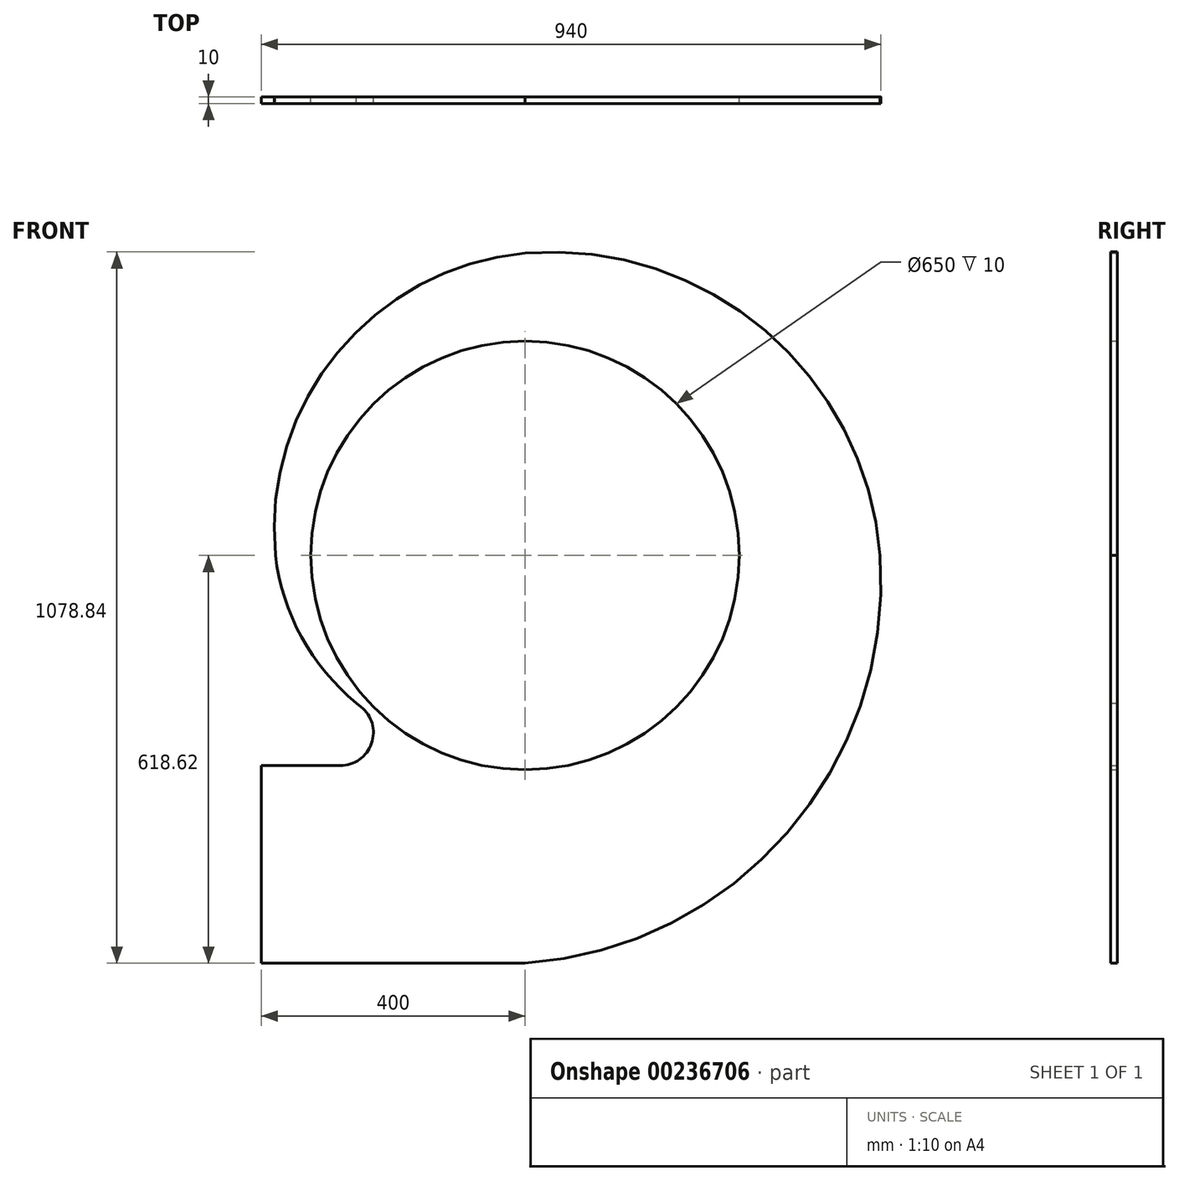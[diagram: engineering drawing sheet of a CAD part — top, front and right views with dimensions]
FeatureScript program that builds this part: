
annotation { "Feature Type Name" : "Feature", "Feature Type Description" : "" }
export const myFeature = defineFeature(function(context is Context, id is Id, definition is map)
    precondition{}
    {
        {
            var Q0;
            Q0=qCreatedBy(makeId("Front.planeOp"),FACE);
            var sketch = newSketch(context, id + "F0", { "sketchPlane" : qUnion([Q0])});
            skLineSegment(sketch, "E0", {"start": v(0, 687.71) * mm, "end": v(0, -665.24) * mm, "construction": true});
            skLineSegment(sketch, "E1", {"start": v(712.27, 0) * mm, "end": v(-772.7, 0) * mm, "construction": true});
            skLineSegment(sketch, "E2", {"start": v(-772.7, 0) * mm, "end": v(-772.7, -643.59) * mm, "construction": true});
            skLineSegment(sketch, "E3", {"start": v(-806.58, -550) * mm, "end": v(762.9, -550) * mm, "construction": true});
            skLineSegment(sketch, "E4", {"start": v(-625.97, -0.99) * mm, "end": v(-621.07, -3.81) * mm});
            skCircle(sketch, "E5", {"center": v(0, 0) * mm, "radius": 320 * mm, "construction": true});
            skLineSegment(sketch, "E6.bottom", {"start": v(-40, 40) * mm, "end": v(40, 40) * mm, "construction": true});
            skLineSegment(sketch, "E6.top", {"start": v(-40, -40) * mm, "end": v(40, -40) * mm, "construction": true});
            skLineSegment(sketch, "E6.left", {"start": v(-40, 40) * mm, "end": v(-40, -40) * mm, "construction": true});
            skLineSegment(sketch, "E6.right", {"start": v(40, 40) * mm, "end": v(40, -40) * mm, "construction": true});
            skArc(sketch, "E7", {"start": v(538.62, 0) * mm, "mid": v(375.2, -444.99) * mm, "end": v(-65.58, -619.44) * mm});
            skArc(sketch, "E8", {"start": v(538.62, 0) * mm, "mid": v(364.3, 340.86) * mm, "end": v(0, 458.62) * mm});
            skArc(sketch, "E9", {"start": v(0, 458.62) * mm, "mid": v(-284.3, 307.72) * mm, "end": v(-378.62, 0) * mm});
            skLineSegment(sketch, "E10", {"start": v(0, -618.62) * mm, "end": v(-400, -618.62) * mm});
            skLineSegment(sketch, "E11", {"start": v(-400, -618.62) * mm, "end": v(-400, -318.62) * mm});
            skLineSegment(sketch, "E12", {"start": v(-400, -318.62) * mm, "end": v(-280.02, -318.62) * mm});
            skLineSegment(sketch, "E13", {"start": v(-248.88, -229.5) * mm, "end": v(-255.85, -223.96) * mm});
            skPoint(sketch, "E14.visualSharp", {"position": v(-136.95, -318.62) * mm});
            skArc(sketch, "E14.filletArc", {"start": v(-280.02, -318.62) * mm, "mid": v(-232.82, -285.11) * mm, "end": v(-248.88, -229.5) * mm});
            skArc(sketch, "E15", {"start": v(-378.62, 0) * mm, "mid": v(-339, -123.9) * mm, "end": v(-255.85, -223.96) * mm});
            skPoint(sketch, "E15.startSnap0", {"position": v(-40, 0) * mm});
            skCircle(sketch, "E16", {"center": v(0, 0) * mm, "radius": 325 * mm});
            skSolve(sketch);
        }
        {
            var Q0;
            Q0=makeQuery(id+"F0.imprint","IMPRINT",FACE,{"disambiguationData":[TD([[makeQuery(id+"F0.imprint","IMPRINT",EDGE,{"derivedFrom":sQuery(id+"F0.wireOp",EDGE,"ZozrHHeU-78oO-nen7-godN-t5K95oYBgX9X")}),1.0]])]});
            var Q1;
            {var subQ1=sQuery(id+"F0.wireOp",EDGE,"E8");Q1=makeQuery(id+"F0.imprint","IMPRINT",FACE,{"disambiguationData":[TD([[makeQuery(id+"F0.imprint","IMPRINT",EDGE,{"derivedFrom":subQ1}),1.0]])]});}
            extrude(context, id + "F1", {"entities" : qUnion([Q0, Q1]), "depth" : 10 * mm, "offsetDistance" : 25 * mm});
        }
    });
